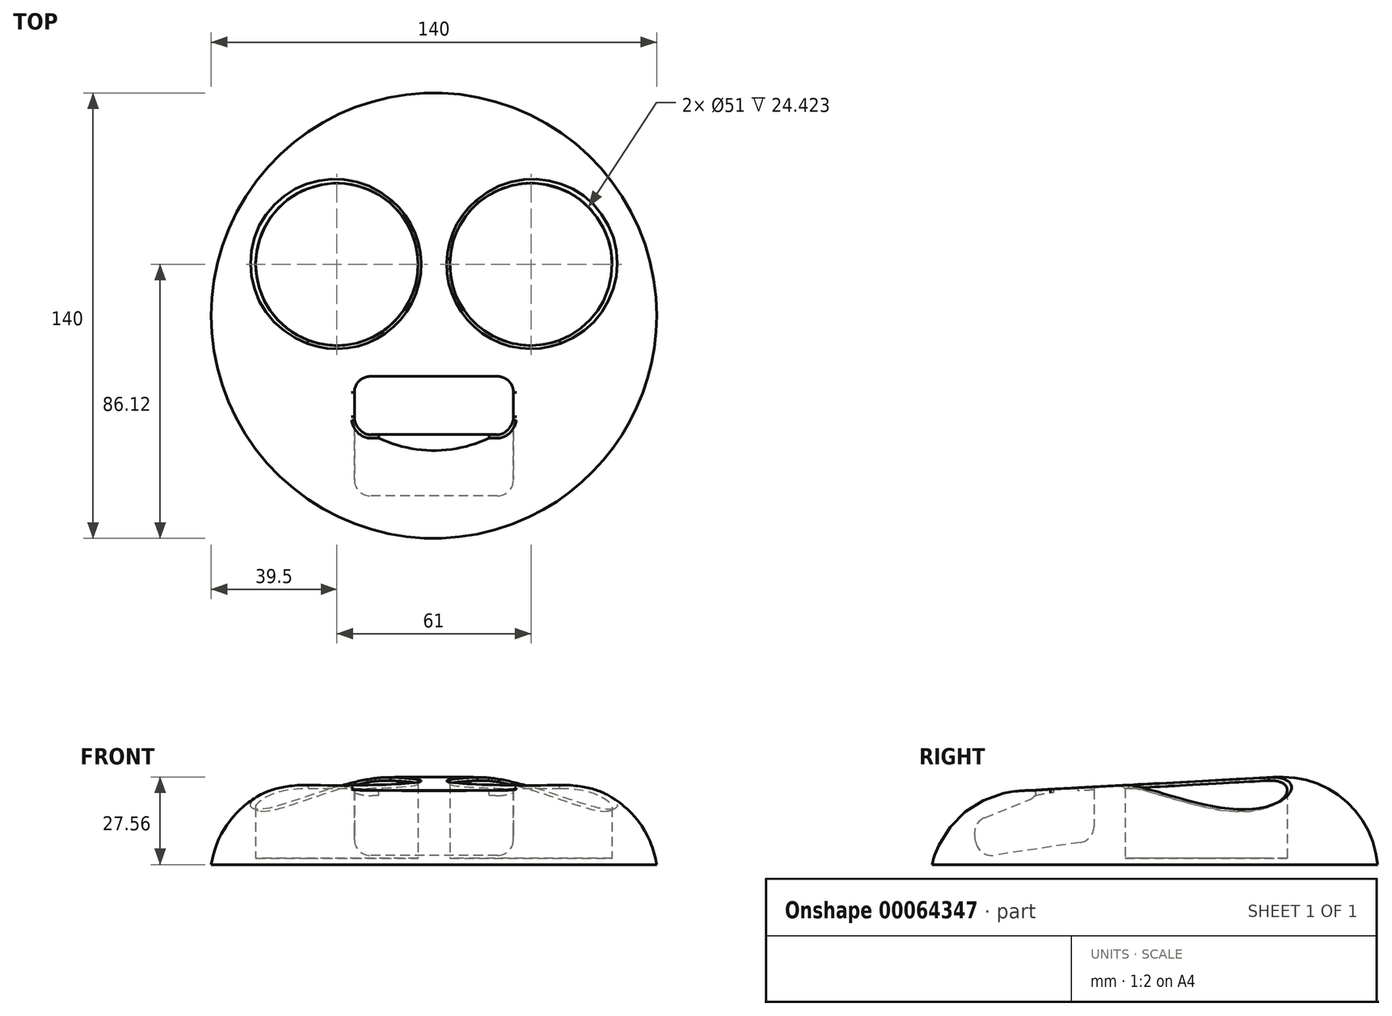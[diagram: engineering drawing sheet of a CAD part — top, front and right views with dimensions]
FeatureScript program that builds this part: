
annotation { "Feature Type Name" : "Feature", "Feature Type Description" : "" }
export const myFeature = defineFeature(function(context is Context, id is Id, definition is map)
    precondition{}
    {
        {
            var Q0;
            Q0=qCreatedBy(makeId("Top.planeOp"),FACE);
            var sketch = newSketch(context, id + "F0", { "sketchPlane" : qUnion([Q0])});
            skCircle(sketch, "E0", {"center": v(-30.5, 0) * mm, "radius": 25.5 * mm});
            skCircle(sketch, "E1", {"center": v(30.5, 0) * mm, "radius": 25.5 * mm});
            skCircle(sketch, "E2", {"center": v(0, -16.12) * mm, "radius": 70 * mm});
            skSolve(sketch);
        }
        {
            var Q0;
            Q0=qCreatedBy(makeId("Top.planeOp"),FACE);
            var sketch = newSketch(context, id + "F1", { "sketchPlane" : qUnion([Q0])});
            skCircle(sketch, "E3.0", {"center": v(0, -16.12) * mm, "radius": 70 * mm});
            skSolve(sketch);
        }
        {
            var Q0;
            Q0=makeQuery(id+"F1.imprint","IMPRINT",FACE,{"disambiguationData":[TD([[makeQuery(id+"F1.imprint","IMPRINT",EDGE,{"derivedFrom":sQuery(id+"F1.wireOp",EDGE,"E3.0")}),1.0]])]});
            var Q1;
            Q1 = qConstructionFilter(qBodyType(qCreatedBy(id + "F1" ,EDGE), BodyType.WIRE), ConstructionObject.NO);
            extrude(context, id + "F2", {"entities" : qUnion([Q0]), "surfaceEntities" : qUnion([Q1]), "depth" : 30 * mm});
        }
        {
            var Q0;
            Q0=qCreatedBy(makeId("Right.planeOp"),FACE);
            var sketch = newSketch(context, id + "F3", { "sketchPlane" : qUnion([Q0])});
            skLineSegment(sketch, "E4", {"start": v(65.8, 29.86) * mm, "end": v(-105.97, 20.61) * mm});
            skLineSegment(sketch, "E5", {"start": v(-105.97, 43.75) * mm, "end": v(-105.97, 20.61) * mm});
            skLineSegment(sketch, "E6", {"start": v(-105.97, 43.75) * mm, "end": v(65.8, 43.75) * mm});
            skLineSegment(sketch, "E7", {"start": v(65.8, 29.86) * mm, "end": v(65.8, 43.75) * mm});
            skSolve(sketch);
        }
        {
            var Q0;
            Q0=makeQuery(id+"F3.imprint","IMPRINT",FACE,{"disambiguationData":[TD([[makeQuery(id+"F3.imprint","IMPRINT",EDGE,{"derivedFrom":sQuery(id+"F3.wireOp",EDGE,"E4")}),-1.0]])]});
            extrude(context, id + "F4", {"entities" : qUnion([Q0]), "operationType" : NewBodyOperationType.REMOVE, "endBound" : BoundingType.SYMMETRIC, "oppositeDirection" : true, "depth" : 150 * mm});
        }
        {
            var Q0;
            Q0=makeQuery(id+"F4.boolean.opBoolean","INTERSECT",EDGE,{"derivedFrom":[makeQuery(id+"F2.opExtrude","SWEPT_FACE",FACE,{"disambiguationData":[OSD([sQuery(id+"F1.wireOp",EDGE,"E3.0")])]}),makeQuery(id+"F4.opExtrude","SWEPT_FACE",FACE,{"disambiguationData":[OSD([sQuery(id+"F3.wireOp",EDGE,"E4")])]})]});
            fillet(context, id + "F5", {"entities" : qUnion([Q0]), "radius" : 30 * mm, "tangentPropagation" : true, "allowEdgeOverflow" : false});
        }
        {
            var Q0;
            Q0=qCreatedBy(makeId("Top.planeOp"),FACE);
            cPlane(context, id + "F6", {"entities" : qUnion([Q0]), "cplaneType" : CPlaneType.OFFSET, "offset" : 2 * mm, "width" : 150 * mm, "height" : 150 * mm});
        }
        {
            var Q0;
            Q0=qCreatedBy(id+"F6.planeOp",FACE);
            var sketch = newSketch(context, id + "F7", { "sketchPlane" : qUnion([Q0])});
            skCircle(sketch, "E8.0", {"center": v(-30.5, 0) * mm, "radius": 25.5 * mm});
            skCircle(sketch, "E8.1", {"center": v(30.5, 0) * mm, "radius": 25.5 * mm});
            skSolve(sketch);
        }
        {
            var Q0;
            Q0 = qSketchRegion(id + "F7", true);
            extrude(context, id + "F8", {"entities" : qUnion([Q0]), "operationType" : NewBodyOperationType.REMOVE, "depth" : 40 * mm});
        }
        {
            var Q0;
            Q0=qCreatedBy(makeId("Right.planeOp"),FACE);
            var sketch = newSketch(context, id + "F9", { "sketchPlane" : qUnion([Q0])});
            skLineSegment(sketch, "E9", {"start": v(-73.3, 13.2) * mm, "end": v(-52.62, 21.54) * mm});
            skLineSegment(sketch, "E10", {"start": v(-52.62, 21.54) * mm, "end": v(-52.62, 36.44) * mm});
            skLineSegment(sketch, "E11", {"start": v(-52.62, 36.44) * mm, "end": v(-35.23, 36.44) * mm});
            skLineSegment(sketch, "E12", {"start": v(-35.23, 36.44) * mm, "end": v(-35.23, 7.6) * mm});
            skLineSegment(sketch, "E13", {"start": v(-35.23, 7.6) * mm, "end": v(-71.62, 2.21) * mm});
            skLineSegment(sketch, "E14", {"start": v(-71.62, 2.21) * mm, "end": v(-73.3, 13.2) * mm});
            skSolve(sketch);
        }
        {
            var Q0;
            Q0=makeQuery(id+"F9.imprint","IMPRINT",FACE,{"disambiguationData":[TD([[makeQuery(id+"F9.imprint","IMPRINT",EDGE,{"derivedFrom":sQuery(id+"F9.wireOp",EDGE,"E9")}),-1.0]])]});
            var Q1;
            Q1=sQuery(id+"F9.wireOp",EDGE,"E11");
            extrude(context, id + "F10", {"entities" : qUnion([Q0]), "surfaceEntities" : qUnion([Q1]), "endBound" : BoundingType.SYMMETRIC, "depth" : 50 * mm});
        }
        {
            var Q0;
            Q0=makeQuery(id+"F10.opExtrude","SWEPT_EDGE",EDGE,{"disambiguationData":[OSD([sQuery(id+"F9.wireOp",EDGE,"E9"),sQuery(id+"F9.wireOp",EDGE,"E10")])]});
            var Q1;
            Q1=makeQuery(id+"F10.opExtrude","SWEPT_EDGE",EDGE,{"disambiguationData":[OSD([sQuery(id+"F9.wireOp",EDGE,"E9"),sQuery(id+"F9.wireOp",EDGE,"E14")])]});
            var Q2;
            Q2=makeQuery(id+"F10.opExtrude","CAP_EDGE",EDGE,{"disambiguationData":[OSD([sQuery(id+"F9.wireOp",EDGE,"E14")])],"isStart":false});
            var Q3;
            Q3=makeQuery(id+"F10.opExtrude","CAP_EDGE",EDGE,{"disambiguationData":[OSD([sQuery(id+"F9.wireOp",EDGE,"E14")])],"isStart":true});
            var Q4;
            Q4=makeQuery(id+"F10.opExtrude","SWEPT_EDGE",EDGE,{"disambiguationData":[OSD([sQuery(id+"F9.wireOp",EDGE,"E13"),sQuery(id+"F9.wireOp",EDGE,"E14")])]});
            var Q5;
            Q5=makeQuery(id+"F10.opExtrude","CAP_EDGE",EDGE,{"disambiguationData":[OSD([sQuery(id+"F9.wireOp",EDGE,"E9")])],"isStart":false});
            var Q6;
            Q6=makeQuery(id+"F10.opExtrude","CAP_EDGE",EDGE,{"disambiguationData":[OSD([sQuery(id+"F9.wireOp",EDGE,"E13")])],"isStart":false});
            var Q7;
            Q7=makeQuery(id+"F10.opExtrude","CAP_EDGE",EDGE,{"disambiguationData":[OSD([sQuery(id+"F9.wireOp",EDGE,"E12")])],"isStart":false});
            var Q8;
            Q8=makeQuery(id+"F10.opExtrude","CAP_EDGE",EDGE,{"disambiguationData":[OSD([sQuery(id+"F9.wireOp",EDGE,"E13")])],"isStart":true});
            var Q9;
            Q9=makeQuery(id+"F10.opExtrude","CAP_EDGE",EDGE,{"disambiguationData":[OSD([sQuery(id+"F9.wireOp",EDGE,"E9")])],"isStart":true});
            var Q10;
            Q10=makeQuery(id+"F10.opExtrude","CAP_EDGE",EDGE,{"disambiguationData":[OSD([sQuery(id+"F9.wireOp",EDGE,"E12")])],"isStart":true});
            var Q11;
            Q11=makeQuery(id+"F10.opExtrude","SWEPT_EDGE",EDGE,{"disambiguationData":[OSD([sQuery(id+"F9.wireOp",EDGE,"E12"),sQuery(id+"F9.wireOp",EDGE,"E13")])]});
            fillet(context, id + "F11", {"entities" : qUnion([Q0, Q1, Q2, Q3, Q4, Q5, Q6, Q7, Q8, Q9, Q10, Q11]), "radius" : 5 * mm, "tangentPropagation" : true, "allowEdgeOverflow" : false});
        }
        {
            var Q0;
            Q0=makeQuery(id+"F10.opExtrude","SWEPT_BODY",BODY,{"disambiguationData":[OSD([sQuery(id+"F9.wireOp",EDGE,"E9"),sQuery(id+"F9.wireOp",EDGE,"E10"),sQuery(id+"F9.wireOp",EDGE,"E11"),sQuery(id+"F9.wireOp",EDGE,"E12"),sQuery(id+"F9.wireOp",EDGE,"E13"),sQuery(id+"F9.wireOp",EDGE,"E14")])]});
            var Q1;
            Q1=makeQuery(id+"F2.opExtrude","SWEPT_BODY",BODY,{"disambiguationData":[OSD([sQuery(id+"F1.wireOp",EDGE,"E3.0")])]});
            booleanBodies(context, id + "F12", {"operationType" : BooleanOperationType.SUBTRACTION, "tools" : qUnion([Q0]), "targets" : qUnion([Q1])});
        }
        {
            var Q0;
            {var subQ0=sQuery(id+"F9.wireOp",EDGE,"E10");var subQ1=sQuery(id+"F9.wireOp",EDGE,"E9");Q0=makeQuery(id+"F12.opBoolean","INTERSECT",EDGE,{"derivedFrom":[makeQuery(id+"F4.boolean.opBoolean","COPY",FACE,{"derivedFrom":makeQuery(id+"F4.opExtrude","SWEPT_FACE",FACE,{"disambiguationData":[OSD([sQuery(id+"F3.wireOp",EDGE,"E4")])]})}),makeQuery(id+"F11.opFillet","BLEND_FACE",FACE,{"disambiguationData":[OSD([subQ1,subQ0]),TDD([makeQuery(id+"F10.opExtrude","SWEPT_EDGE",EDGE,{"disambiguationData":[OSD([subQ1,subQ0])]})])]})]});}
            fillet(context, id + "F13", {"entities" : qUnion([Q0]), "radius" : 1 * mm, "tangentPropagation" : true, "allowEdgeOverflow" : false});
        }
        {
            var Q0;
            Q0=makeQuery(id+"F8.boolean.opBoolean","INTERSECT",EDGE,{"derivedFrom":[makeQuery(id+"F5.opFillet","BLEND_FACE",FACE,{"disambiguationData":[OSD([sQuery(id+"F1.wireOp",EDGE,"E3.0"),sQuery(id+"F3.wireOp",EDGE,"E4")])]}),makeQuery(id+"F8.opExtrude","SWEPT_FACE",FACE,{"disambiguationData":[OSD([sQuery(id+"F7.wireOp",EDGE,"E8.0")])]})]});
            var Q1;
            Q1=makeQuery(id+"F8.boolean.opBoolean","INTERSECT",EDGE,{"derivedFrom":[makeQuery(id+"F4.boolean.opBoolean","COPY",FACE,{"derivedFrom":makeQuery(id+"F4.opExtrude","SWEPT_FACE",FACE,{"disambiguationData":[OSD([sQuery(id+"F3.wireOp",EDGE,"E4")])]})}),makeQuery(id+"F8.opExtrude","SWEPT_FACE",FACE,{"disambiguationData":[OSD([sQuery(id+"F7.wireOp",EDGE,"E8.0")])]})]});
            var Q2;
            Q2=makeQuery(id+"F8.boolean.opBoolean","INTERSECT",EDGE,{"derivedFrom":[makeQuery(id+"F4.boolean.opBoolean","COPY",FACE,{"derivedFrom":makeQuery(id+"F4.opExtrude","SWEPT_FACE",FACE,{"disambiguationData":[OSD([sQuery(id+"F3.wireOp",EDGE,"E4")])]})}),makeQuery(id+"F8.opExtrude","SWEPT_FACE",FACE,{"disambiguationData":[OSD([sQuery(id+"F7.wireOp",EDGE,"E8.1")])]})]});
            var Q3;
            Q3=makeQuery(id+"F8.boolean.opBoolean","INTERSECT",EDGE,{"derivedFrom":[makeQuery(id+"F5.opFillet","BLEND_FACE",FACE,{"disambiguationData":[OSD([sQuery(id+"F1.wireOp",EDGE,"E3.0"),sQuery(id+"F3.wireOp",EDGE,"E4")])]}),makeQuery(id+"F8.opExtrude","SWEPT_FACE",FACE,{"disambiguationData":[OSD([sQuery(id+"F7.wireOp",EDGE,"E8.1")])]})]});
            chamfer(context, id + "F14", {"entities" : qUnion([Q0, Q1, Q2, Q3]), "width" : 1 * mm, "tangentPropagation" : true});
        }
    });
